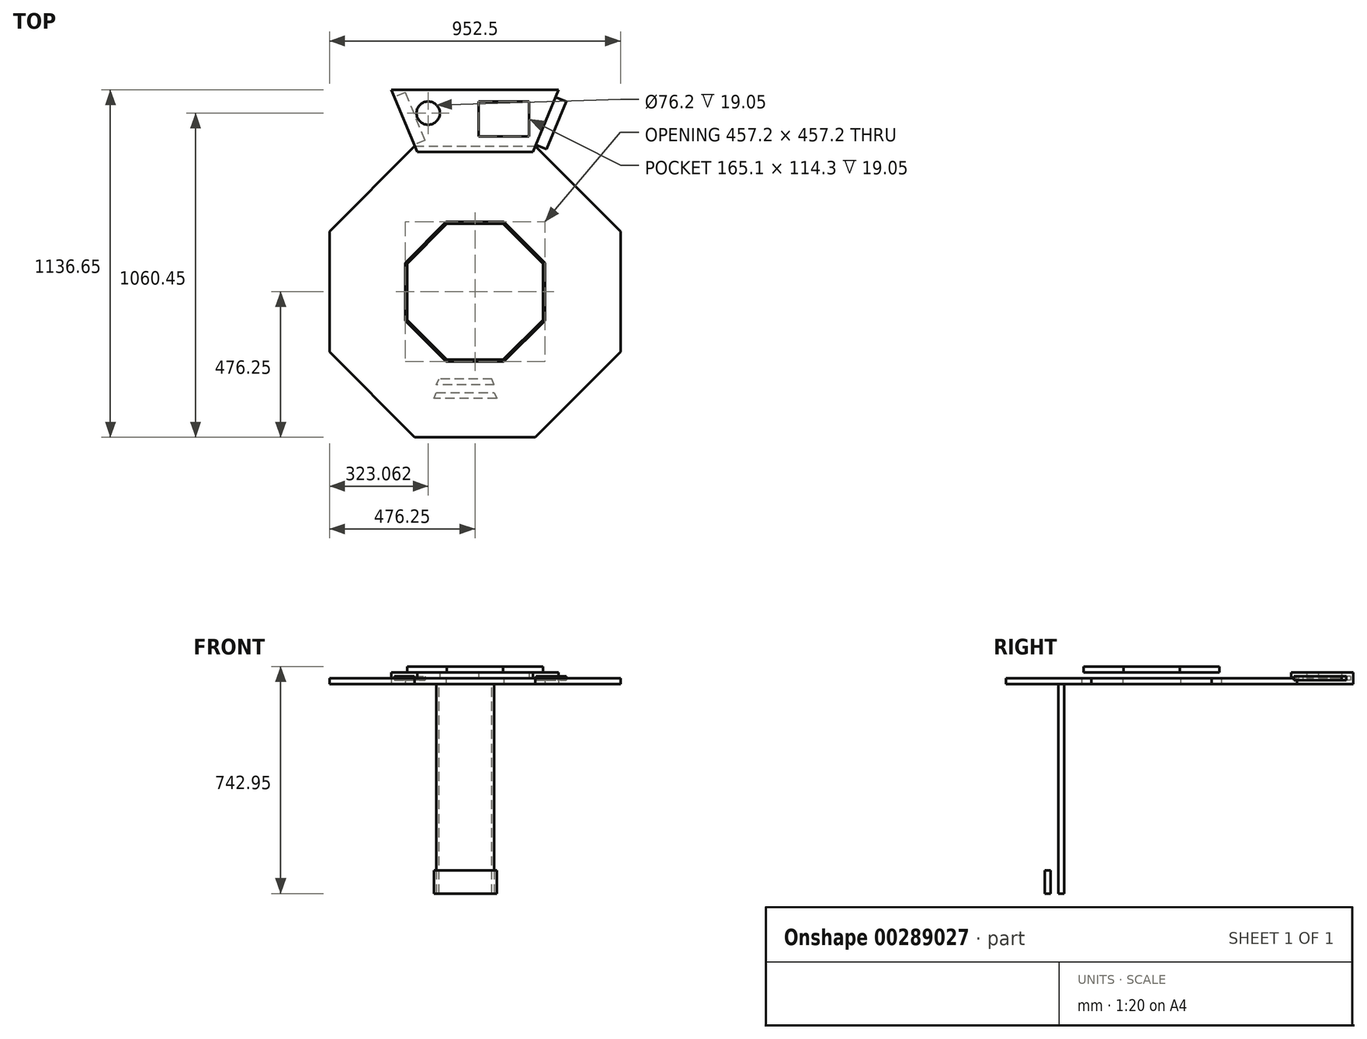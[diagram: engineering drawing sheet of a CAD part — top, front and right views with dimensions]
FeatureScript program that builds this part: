
annotation { "Feature Type Name" : "Feature", "Feature Type Description" : "" }
export const myFeature = defineFeature(function(context is Context, id is Id, definition is map)
    precondition{}
    {
        {
            var Q0;
            Q0=qCreatedBy(makeId("Top.planeOp"),FACE);
            var sketch = newSketch(context, id + "F0", { "sketchPlane" : qUnion([Q0])});
            skLineSegment(sketch, "E0.4", {"start": v(-273.55, 660.4) * mm, "end": v(273.55, 660.4) * mm});
            skLineSegment(sketch, "E1.4", {"start": v(-189.38, 457.2) * mm, "end": v(189.38, 457.2) * mm});
            skLineSegment(sketch, "E2", {"start": v(-273.55, 660.4) * mm, "end": v(-189.38, 457.2) * mm});
            skLineSegment(sketch, "E3", {"start": v(273.55, 660.4) * mm, "end": v(189.38, 457.2) * mm});
            skLineSegment(sketch, "E4.bottom", {"start": v(11.91, 622.3) * mm, "end": v(177.01, 622.3) * mm});
            skLineSegment(sketch, "E4.top", {"start": v(11.91, 508) * mm, "end": v(177.01, 508) * mm});
            skLineSegment(sketch, "E4.left", {"start": v(11.91, 622.3) * mm, "end": v(11.91, 508) * mm});
            skLineSegment(sketch, "E4.right", {"start": v(177.01, 622.3) * mm, "end": v(177.01, 508) * mm});
            skCircle(sketch, "E5", {"center": v(-153.19, 584.2) * mm, "radius": 38.1 * mm});
            skSolve(sketch);
        }
        {
            var Q0;
            Q0=makeQuery(id+"F0.imprint","IMPRINT",FACE,{"disambiguationData":[TD([[makeQuery(id+"F0.imprint","IMPRINT",EDGE,{"derivedFrom":sQuery(id+"F0.wireOp",EDGE,"E0.4")}),-1.0]])]});
            extrude(context, id + "F1", {"entities" : qUnion([Q0]), "depth" : 38.1 * mm});
        }
        {
            var Q0;
            Q0=makeQuery(id+"F1.opExtrude","SWEPT_FACE",FACE,{"disambiguationData":[OSD([sQuery(id+"F0.wireOp",EDGE,"E2")])]});
            var sketch = newSketch(context, id + "F2", { "sketchPlane" : qUnion([Q0])});
            skLineSegment(sketch, "E6.bottom", {"start": v(-689.41, 25.4) * mm, "end": v(-520.27, 25.4) * mm});
            skLineSegment(sketch, "E6.top", {"start": v(-689.41, 12.7) * mm, "end": v(-520.27, 12.7) * mm});
            skLineSegment(sketch, "E6.left", {"start": v(-689.41, 25.4) * mm, "end": v(-689.41, 12.7) * mm});
            skLineSegment(sketch, "E6.right", {"start": v(-520.27, 25.4) * mm, "end": v(-520.27, 12.7) * mm});
            skSolve(sketch);
        }
        {
            var Q0;
            Q0=makeQuery(id+"F2.imprint","IMPRINT",FACE,{"disambiguationData":[TD([[makeQuery(id+"F2.imprint","IMPRINT",EDGE,{"derivedFrom":sQuery(id+"F2.wireOp",EDGE,"E6.bottom")}),-1.0]])]});
            extrude(context, id + "F3", {"entities" : qUnion([Q0]), "operationType" : NewBodyOperationType.REMOVE, "oppositeDirection" : true, "depth" : 38.1 * mm});
        }
        {
            var Q0;
            Q0=makeQuery(id+"F1.opExtrude","SWEPT_FACE",FACE,{"disambiguationData":[OSD([sQuery(id+"F0.wireOp",EDGE,"E3")])]});
            var sketch = newSketch(context, id + "F4", { "sketchPlane" : qUnion([Q0])});
            skLineSegment(sketch, "E7.bottom", {"start": v(520.27, 25.4) * mm, "end": v(689.41, 25.4) * mm});
            skLineSegment(sketch, "E7.top", {"start": v(520.27, 12.7) * mm, "end": v(689.41, 12.7) * mm});
            skLineSegment(sketch, "E7.left", {"start": v(520.27, 25.4) * mm, "end": v(520.27, 12.7) * mm});
            skLineSegment(sketch, "E7.right", {"start": v(689.41, 25.4) * mm, "end": v(689.41, 12.7) * mm});
            skSolve(sketch);
        }
        {
            var Q0;
            Q0=makeQuery(id+"F4.imprint","IMPRINT",FACE,{"disambiguationData":[TD([[makeQuery(id+"F4.imprint","IMPRINT",EDGE,{"derivedFrom":sQuery(id+"F4.wireOp",EDGE,"E7.bottom")}),-1.0]])]});
            extrude(context, id + "F5", {"entities" : qUnion([Q0]), "operationType" : NewBodyOperationType.ADD, "depth" : 38.1 * mm});
        }
        {
            var Q0;
            Q0=makeQuery(id+"F0.imprint","IMPRINT",FACE,{"disambiguationData":[TD([[makeQuery(id+"F0.imprint","IMPRINT",EDGE,{"derivedFrom":sQuery(id+"F0.wireOp",EDGE,"E0.4")}),-1.0]])]});
            var sketch = newSketch(context, id + "F6", { "sketchPlane" : qUnion([Q0])});
            skLineSegment(sketch, "E8.bottom", {"start": v(-197.27, 457.2) * mm, "end": v(197.27, 457.2) * mm});
            skLineSegment(sketch, "E8.top", {"start": v(-197.27, 476.25) * mm, "end": v(197.27, 476.25) * mm});
            skLineSegment(sketch, "E8.left", {"start": v(-197.27, 457.2) * mm, "end": v(-197.27, 476.25) * mm});
            skLineSegment(sketch, "E8.right", {"start": v(197.27, 457.2) * mm, "end": v(197.27, 476.25) * mm});
            skSolve(sketch);
        }
        {
            var Q0;
            {var subQ5=sQuery(id+"F6.wireOp",EDGE,"E8.top");Q0=makeQuery(id+"F6.imprint","IMPRINT",FACE,{"disambiguationData":[TD([[makeQuery(id+"F6.imprint","IMPRINT",EDGE,{"derivedFrom":subQ5}),-1.0]])]});}
            extrude(context, id + "F7", {"entities" : qUnion([Q0]), "operationType" : NewBodyOperationType.REMOVE, "depth" : 19.05 * mm});
        }
        {
            var Q0;
            Q0=qCreatedBy(makeId("Top.planeOp"),FACE);
            var sketch = newSketch(context, id + "F8", { "sketchPlane" : qUnion([Q0])});
            skCircle(sketch, "E9.cCircle", {"center": v(0, 0) * mm, "radius": 476.25 * mm, "construction": true});
            skPoint(sketch, "E9.cCircle.perimeterSnap0", {"position": v(0, 457.2) * mm});
            skLineSegment(sketch, "E9.0", {"start": v(197.27, -476.25) * mm, "end": v(-197.27, -476.25) * mm});
            skLineSegment(sketch, "E9.1", {"start": v(-197.27, -476.25) * mm, "end": v(-476.25, -197.27) * mm});
            skLineSegment(sketch, "E9.2", {"start": v(-476.25, -197.27) * mm, "end": v(-476.25, 197.27) * mm});
            skLineSegment(sketch, "E9.3", {"start": v(-476.25, 197.27) * mm, "end": v(-197.27, 476.25) * mm});
            skLineSegment(sketch, "E9.4", {"start": v(-197.27, 476.25) * mm, "end": v(197.27, 476.25) * mm});
            skLineSegment(sketch, "E9.5", {"start": v(197.27, 476.25) * mm, "end": v(476.25, 197.27) * mm});
            skLineSegment(sketch, "E9.6", {"start": v(476.25, 197.27) * mm, "end": v(476.25, -197.27) * mm});
            skLineSegment(sketch, "E9.7", {"start": v(476.25, -197.27) * mm, "end": v(197.27, -476.25) * mm});
            skPoint(sketch, "E9.0.midPoint", {"position": v(0, -476.25) * mm});
            skPoint(sketch, "E9.0.midPoint.positionSnap0", {"position": v(0, 457.2) * mm});
            skCircle(sketch, "E10.cCircle", {"center": v(0, 0) * mm, "radius": 228.6 * mm, "construction": true});
            skLineSegment(sketch, "E10.0", {"start": v(94.69, -228.6) * mm, "end": v(-94.69, -228.6) * mm});
            skLineSegment(sketch, "E10.1", {"start": v(-94.69, -228.6) * mm, "end": v(-228.6, -94.69) * mm});
            skLineSegment(sketch, "E10.2", {"start": v(-228.6, -94.69) * mm, "end": v(-228.6, 94.69) * mm});
            skLineSegment(sketch, "E10.3", {"start": v(-228.6, 94.69) * mm, "end": v(-94.69, 228.6) * mm});
            skLineSegment(sketch, "E10.4", {"start": v(-94.69, 228.6) * mm, "end": v(94.69, 228.6) * mm});
            skLineSegment(sketch, "E10.5", {"start": v(94.69, 228.6) * mm, "end": v(228.6, 94.69) * mm});
            skLineSegment(sketch, "E10.6", {"start": v(228.6, 94.69) * mm, "end": v(228.6, -94.69) * mm});
            skLineSegment(sketch, "E10.7", {"start": v(228.6, -94.69) * mm, "end": v(94.69, -228.6) * mm});
            skPoint(sketch, "E10.0.midPoint", {"position": v(0, -228.6) * mm});
            skSolve(sketch);
        }
        {
            var Q0;
            Q0=makeQuery(id+"F8.imprint","IMPRINT",FACE,{"disambiguationData":[TD([[makeQuery(id+"F8.imprint","IMPRINT",EDGE,{"derivedFrom":sQuery(id+"F8.wireOp",EDGE,"E9.1")}),-1.0]])]});
            extrude(context, id + "F9", {"entities" : qUnion([Q0]), "depth" : 19.05 * mm});
        }
        {
            var Q0;
            Q0=qCreatedBy(makeId("Top.planeOp"),FACE);
            var sketch = newSketch(context, id + "F10", { "sketchPlane" : qUnion([Q0])});
            skLineSegment(sketch, "E11.4", {"start": v(63.13, -304.8) * mm, "end": v(-126.25, -304.8) * mm});
            skLineSegment(sketch, "E12.4", {"start": v(55.23, -285.75) * mm, "end": v(-118.36, -285.75) * mm});
            skLineSegment(sketch, "E13", {"start": v(-126.25, -304.8) * mm, "end": v(-118.36, -285.75) * mm});
            skLineSegment(sketch, "E14", {"start": v(63.13, -304.8) * mm, "end": v(55.23, -285.75) * mm});
            skSolve(sketch);
        }
        {
            var Q0;
            Q0=makeQuery(id+"F10.imprint","IMPRINT",FACE,{"disambiguationData":[TD([[makeQuery(id+"F10.imprint","IMPRINT",EDGE,{"derivedFrom":sQuery(id+"F10.wireOp",EDGE,"E11.4")}),-1.0]])]});
            extrude(context, id + "F11", {"entities" : qUnion([Q0]), "oppositeDirection" : true, "depth" : 685.8 * mm});
        }
        {
            var Q0;
            Q0=makeQuery(id+"F1.opExtrude","CAP_FACE",FACE,{"disambiguationData":[OSD([sQuery(id+"F0.wireOp",EDGE,"E0.4"),sQuery(id+"F0.wireOp",EDGE,"E1.4"),sQuery(id+"F0.wireOp",EDGE,"E2"),sQuery(id+"F0.wireOp",EDGE,"E3")])],"isStart":false});
            var sketch = newSketch(context, id + "F12", { "sketchPlane" : qUnion([Q0])});
            skCircle(sketch, "E15.cCircle", {"center": v(0, 0) * mm, "radius": 222.25 * mm, "construction": true});
            skLineSegment(sketch, "E15.0", {"start": v(92.06, -222.25) * mm, "end": v(-92.06, -222.25) * mm});
            skLineSegment(sketch, "E15.1", {"start": v(-92.06, -222.25) * mm, "end": v(-222.25, -92.06) * mm});
            skLineSegment(sketch, "E15.2", {"start": v(-222.25, -92.06) * mm, "end": v(-222.25, 92.06) * mm});
            skLineSegment(sketch, "E15.3", {"start": v(-222.25, 92.06) * mm, "end": v(-92.06, 222.25) * mm});
            skLineSegment(sketch, "E15.4", {"start": v(-92.06, 222.25) * mm, "end": v(92.06, 222.25) * mm});
            skLineSegment(sketch, "E15.5", {"start": v(92.06, 222.25) * mm, "end": v(222.25, 92.06) * mm});
            skLineSegment(sketch, "E15.6", {"start": v(222.25, 92.06) * mm, "end": v(222.25, -92.06) * mm});
            skLineSegment(sketch, "E15.7", {"start": v(222.25, -92.06) * mm, "end": v(92.06, -222.25) * mm});
            skPoint(sketch, "E15.0.midPoint", {"position": v(0, -222.25) * mm});
            skSolve(sketch);
        }
        {
            var Q0;
            Q0 = qSketchRegion(id + "F12", true);
            extrude(context, id + "F13", {"entities" : qUnion([Q0]), "depth" : 19.05 * mm});
        }
        {
            var Q0;
            Q0=makeQuery(id+"F11.opExtrude","CAP_FACE",FACE,{"disambiguationData":[OSD([sQuery(id+"F10.wireOp",EDGE,"E11.4"),sQuery(id+"F10.wireOp",EDGE,"E12.4"),sQuery(id+"F10.wireOp",EDGE,"E13"),sQuery(id+"F10.wireOp",EDGE,"E14")])],"isStart":false});
            var sketch = newSketch(context, id + "F14", { "sketchPlane" : qUnion([Q0])});
            skLineSegment(sketch, "E16", {"start": v(-126.25, 330.2) * mm, "end": v(63.13, 330.2) * mm});
            skLineSegment(sketch, "E17", {"start": v(63.13, 330.2) * mm, "end": v(71.02, 349.25) * mm});
            skLineSegment(sketch, "E18", {"start": v(71.02, 349.25) * mm, "end": v(-134.14, 349.25) * mm});
            skLineSegment(sketch, "E19", {"start": v(-134.14, 349.25) * mm, "end": v(-126.25, 330.2) * mm});
            skSolve(sketch);
        }
        {
            var Q0;
            Q0=makeQuery(id+"F14.imprint","IMPRINT",FACE,{"disambiguationData":[TD([[makeQuery(id+"F14.imprint","IMPRINT",EDGE,{"derivedFrom":sQuery(id+"F14.wireOp",EDGE,"E16")}),1.0]])]});
            extrude(context, id + "F15", {"entities" : qUnion([Q0]), "oppositeDirection" : true, "depth" : 76.2 * mm});
        }
        {
            var Q0;
            Q0=makeQuery(id+"F0.imprint","IMPRINT",FACE,{"disambiguationData":[TD([[makeQuery(id+"F0.imprint","IMPRINT",EDGE,{"derivedFrom":sQuery(id+"F0.wireOp",EDGE,"E5")}),1.0]])]});
            var Q1;
            Q1=makeQuery(id+"F0.imprint","IMPRINT",FACE,{"disambiguationData":[TD([[makeQuery(id+"F0.imprint","IMPRINT",EDGE,{"derivedFrom":sQuery(id+"F0.wireOp",EDGE,"E4.bottom")}),-1.0]])]});
            extrude(context, id + "F16", {"entities" : qUnion([Q0, Q1]), "operationType" : NewBodyOperationType.ADD, "depth" : 19.05 * mm});
        }
    });
